# Revit family: Haworth_Luxor_Cabinet_28
name_source: partatom
category: Furniture
revit_build: Autodesk Revit 2018 (Build: 20170223_1515(x64)
units: mm (PartAtom-declared; Revit-internal decimal feet)

## family parameters
Always vertical = Yes
Cut with Voids When Loaded = No
OmniClass Number = 23.40.20.00
OmniClass Title = General Furniture and Specialties
Room Calculation Point = No
Shared = No
Work Plane-Based = No

## types (7) — shared parameters
Assembly Code = E2020200
Description = Haworth Luxor Cabinet 28
Manufacturer = Haworth
Model = HCCE-LX
Size = Verify Final Dim. w/ Haworth
URL = http://www.haworth.com
URL - Product = https://www.haworth.com
Version = 2
Warranty = http://www.haworth.com

## per-type parameters (varying)
| type | 2 Compartments | 3 Compartments | Actual Height | Actual Width | Doors | Height 35.5in | Height 52in | Number of Doors | Open | Three Door | Two Door |
| HCCE-LX - Shelf & Two Drawers/Door - 71w 35h | Yes | No | 2' - 11 1/2" | 5' - 10 3/4" | Yes | Yes | No | 2 | No | No | Yes |
| HCCE-LX - Door/Shelf & Two Drawers/Door - 106w 35h | No | Yes | 2' - 11 1/2" | 8' - 10 1/4" | Yes | Yes | No | 2 | Yes | No | Yes |
| HCCE-LX - Door/Shelf & Drawer/Door - 106w 35h | No | Yes | 2' - 11 1/2" | 8' - 10 1/4" | Yes | Yes | No | 3 | No | Yes | No |
| HCCE-LX - Open - 71w 52h | Yes | No | 4' - 4" | 5' - 10 3/4" | No | No | Yes | 2 | Yes | No | No |
| HCCE-LX - Open & Two Drawers/Door - 71w 52h | Yes | No | 4' - 4" | 5' - 10 3/4" | Yes | No | Yes | 2 | No | No | Yes |
| HCCE-LX - Door/Open/Door - 106w 52h | No | Yes | 4' - 4" | 8' - 10 1/4" | Yes | No | Yes | 2 | Yes | No | Yes |
| HCCE-LX - Door/Open & Drawer/Door - 106w 52h | No | Yes | 4' - 4" | 8' - 10 1/4" | Yes | No | Yes | 3 | No | Yes | No |

## geometry (parser evidence)
native form markers: Blend x4, Sweep x11
no freeform markers — native parametric forms only
